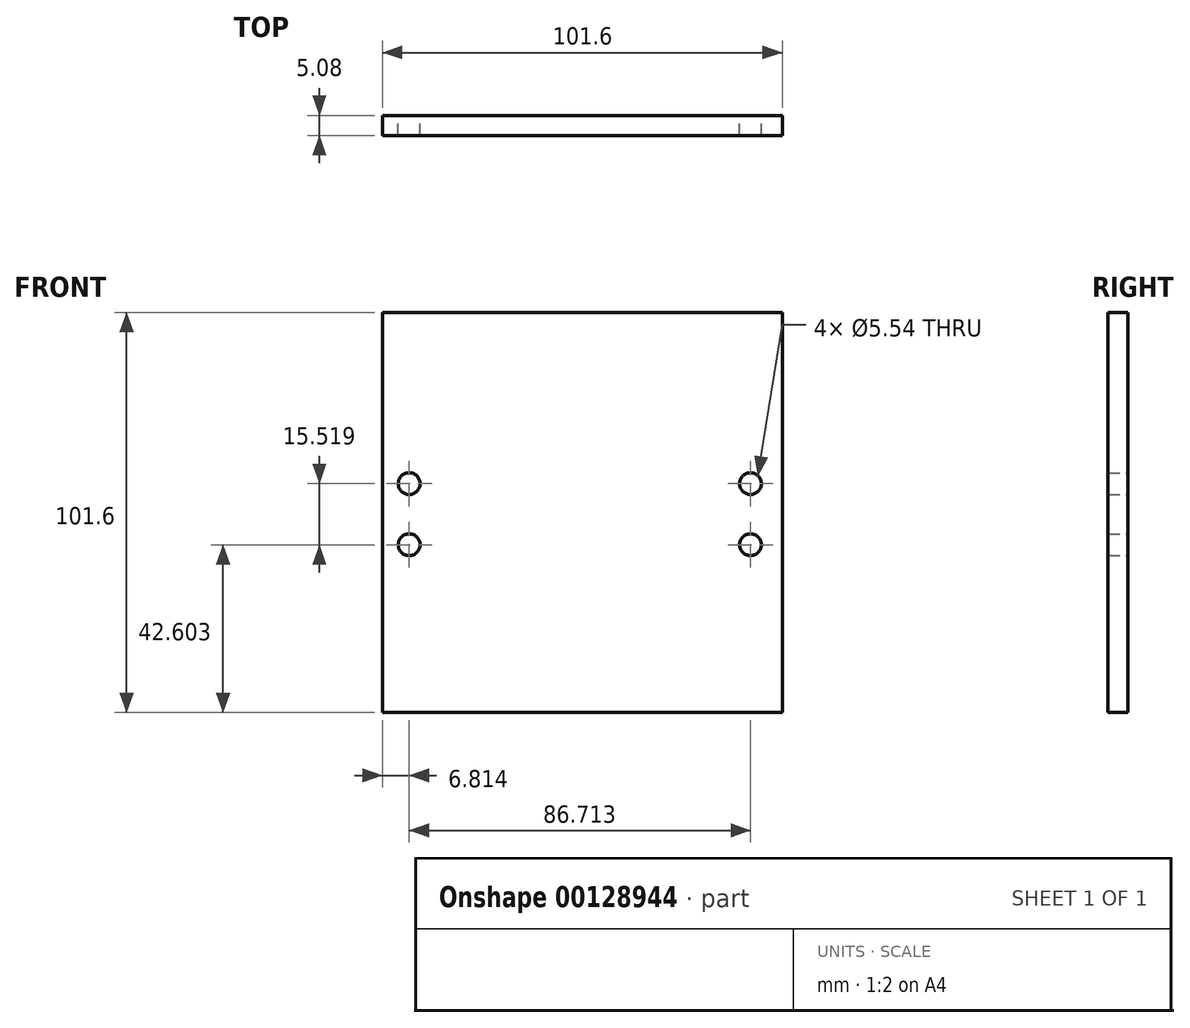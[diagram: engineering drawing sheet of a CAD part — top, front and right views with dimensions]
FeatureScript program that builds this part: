
annotation { "Feature Type Name" : "Feature", "Feature Type Description" : "" }
export const myFeature = defineFeature(function(context is Context, id is Id, definition is map)
    precondition{}
    {
        {
            var Q0;
            Q0=qCreatedBy(makeId("Front.planeOp"),FACE);
            var sketch = newSketch(context, id + "F0", { "sketchPlane" : qUnion([Q0])});
            skLineSegment(sketch, "E0.bottom", {"start": v(-38.53, 66.04) * mm, "end": v(63.07, 66.04) * mm});
            skLineSegment(sketch, "E0.top", {"start": v(-38.53, -35.56) * mm, "end": v(63.07, -35.56) * mm});
            skLineSegment(sketch, "E0.left", {"start": v(-38.53, 66.04) * mm, "end": v(-38.53, -35.56) * mm});
            skLineSegment(sketch, "E0.right", {"start": v(63.07, 66.04) * mm, "end": v(63.07, -35.56) * mm});
            skCircle(sketch, "E1", {"center": v(55, 7.04) * mm, "radius": 2.77 * mm});
            skCircle(sketch, "E2", {"center": v(55, 22.56) * mm, "radius": 2.77 * mm});
            skCircle(sketch, "E3", {"center": v(-31.72, 7.04) * mm, "radius": 2.77 * mm});
            skCircle(sketch, "E4", {"center": v(-31.72, 22.56) * mm, "radius": 2.77 * mm});
            skSolve(sketch);
        }
        {
            var Q0;
            Q0 = qSketchRegion(id + "F0", true);
            extrude(context, id + "F1", {"entities" : qUnion([Q0]), "depth" : 5.08 * mm});
        }
        {
            var Q0;
            Q0 = qSketchRegion(id + "F0", true);
            extrude(context, id + "F2", {"entities" : qUnion([Q0]), "operationType" : NewBodyOperationType.ADD, "depth" : 5.08 * mm});
        }
    });
